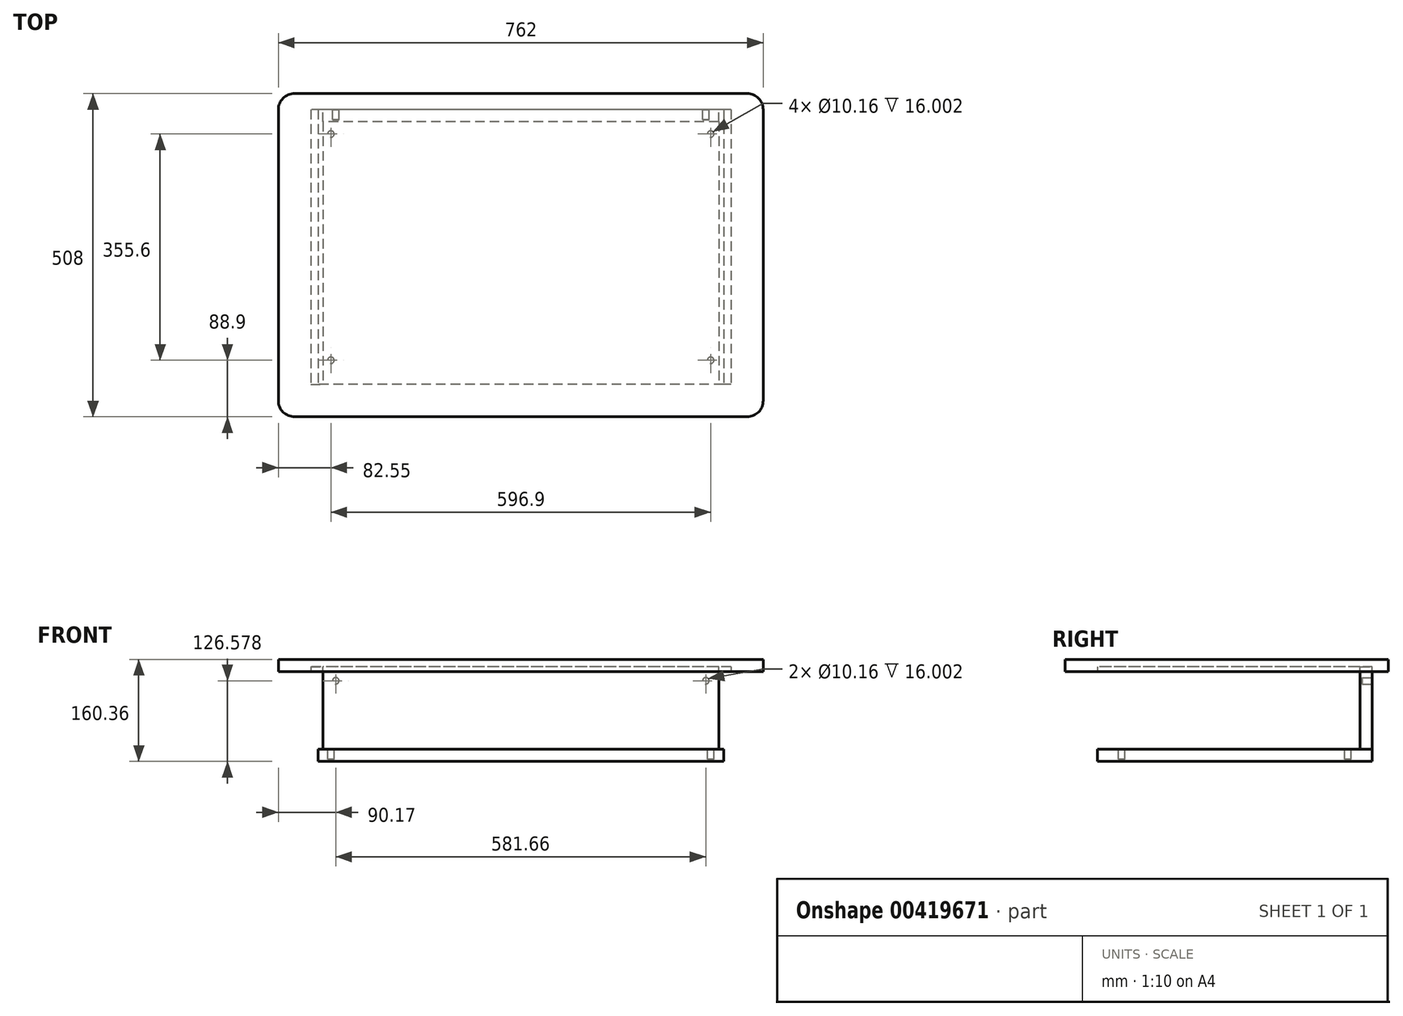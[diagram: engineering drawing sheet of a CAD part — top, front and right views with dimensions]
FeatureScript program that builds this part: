
annotation { "Feature Type Name" : "Feature", "Feature Type Description" : "" }
export const myFeature = defineFeature(function(context is Context, id is Id, definition is map)
    precondition{}
    {
        {
            var Q0;
            Q0=qCreatedBy(makeId("Top.planeOp"),FACE);
            var sketch = newSketch(context, id + "F0", { "sketchPlane" : qUnion([Q0])});
            skLineSegment(sketch, "E0.bottom", {"start": v(-355.6, 254) * mm, "end": v(355.6, 254) * mm});
            skLineSegment(sketch, "E0.top", {"start": v(-355.6, -254) * mm, "end": v(355.6, -254) * mm});
            skLineSegment(sketch, "E0.left", {"start": v(-381, 228.6) * mm, "end": v(-381, -228.6) * mm});
            skLineSegment(sketch, "E0.right", {"start": v(381, 228.6) * mm, "end": v(381, -228.6) * mm});
            skPoint(sketch, "E0.middle", {"position": v(0, 0) * mm});
            skPoint(sketch, "E1.visualSharp", {"position": v(381, 254) * mm});
            skArc(sketch, "E1.filletArc", {"start": v(381, 228.6) * mm, "mid": v(373.56, 246.56) * mm, "end": v(355.6, 254) * mm});
            skPoint(sketch, "E2.visualSharp", {"position": v(381, -254) * mm});
            skArc(sketch, "E2.filletArc", {"start": v(355.6, -254) * mm, "mid": v(373.56, -246.56) * mm, "end": v(381, -228.6) * mm});
            skPoint(sketch, "E3.visualSharp", {"position": v(-381, -254) * mm});
            skArc(sketch, "E3.filletArc", {"start": v(-381, -228.6) * mm, "mid": v(-373.56, -246.56) * mm, "end": v(-355.6, -254) * mm});
            skPoint(sketch, "E4.visualSharp", {"position": v(-381, 254) * mm});
            skArc(sketch, "E4.filletArc", {"start": v(-355.6, 254) * mm, "mid": v(-373.56, 246.56) * mm, "end": v(-381, 228.6) * mm});
            skSolve(sketch);
        }
        {
            var Q0;
            Q0=qSketchRegion(id+"F0",true);
            extrude(context, id + "F1", {"entities" : qUnion([Q0]), "depth" : 19.05 * mm, "offsetDistance" : 25.4 * mm});
        }
        {
            var Q0;
            Q0=makeQuery(id+"F1.opExtrude","CAP_FACE",FACE,{"disambiguationData":[OSD([sQuery(id+"F0.wireOp",EDGE,"E0.bottom"),sQuery(id+"F0.wireOp",EDGE,"E0.top"),sQuery(id+"F0.wireOp",EDGE,"E0.left"),sQuery(id+"F0.wireOp",EDGE,"E0.right"),sQuery(id+"F0.wireOp",EDGE,"E1.filletArc"),sQuery(id+"F0.wireOp",EDGE,"E2.filletArc"),sQuery(id+"F0.wireOp",EDGE,"E3.filletArc"),sQuery(id+"F0.wireOp",EDGE,"E4.filletArc")])],"isStart":true});
            var sketch = newSketch(context, id + "F2", { "sketchPlane" : qUnion([Q0])});
            skLineSegment(sketch, "E5.bottom", {"start": v(330.2, -228.6) * mm, "end": v(-330.2, -228.6) * mm});
            skLineSegment(sketch, "E5.top", {"start": v(330.2, -209.55) * mm, "end": v(-330.2, -209.55) * mm});
            skLineSegment(sketch, "E5.left", {"start": v(330.2, -228.6) * mm, "end": v(330.2, -209.55) * mm});
            skLineSegment(sketch, "E5.right", {"start": v(-330.2, -228.6) * mm, "end": v(-330.2, -209.55) * mm});
            skLineSegment(sketch, "E6.top", {"start": v(330.2, 203.2) * mm, "end": v(311.15, 203.2) * mm});
            skLineSegment(sketch, "E6.left", {"start": v(330.2, -209.55) * mm, "end": v(330.2, 203.2) * mm});
            skLineSegment(sketch, "E6.right", {"start": v(311.15, -209.55) * mm, "end": v(311.15, 203.2) * mm});
            skLineSegment(sketch, "E7.bottom", {"start": v(-330.2, -209.55) * mm, "end": v(-311.15, -209.55) * mm});
            skLineSegment(sketch, "E7.top", {"start": v(-330.2, 203.2) * mm, "end": v(-311.15, 203.2) * mm});
            skLineSegment(sketch, "E7.left", {"start": v(-330.2, -209.55) * mm, "end": v(-330.2, 203.2) * mm});
            skLineSegment(sketch, "E7.right", {"start": v(-311.15, -209.55) * mm, "end": v(-311.15, 203.2) * mm});
            skSolve(sketch);
        }
        {
            var Q0;
            Q0=qSketchRegion(id+"F2",true);
            extrude(context, id + "F3", {"entities" : qUnion([Q0]), "operationType" : NewBodyOperationType.REMOVE, "oppositeDirection" : true, "depth" : 7.62 * mm});
        }
        {
            var Q0;
            Q0=makeQuery(id+"F3.boolean.opBoolean","COPY",FACE,{"derivedFrom":makeQuery(id+"F3.opExtrude","CAP_FACE",FACE,{"disambiguationData":[OSD([sQuery(id+"F2.wireOp",EDGE,"E5.bottom"),sQuery(id+"F2.wireOp",EDGE,"E5.top"),sQuery(id+"F2.wireOp",EDGE,"E5.left"),sQuery(id+"F2.wireOp",EDGE,"E5.right"),sQuery(id+"F2.wireOp",EDGE,"E6.top"),sQuery(id+"F2.wireOp",EDGE,"E6.left"),sQuery(id+"F2.wireOp",EDGE,"E6.right"),sQuery(id+"F2.wireOp",EDGE,"E7.top"),sQuery(id+"F2.wireOp",EDGE,"E7.left"),sQuery(id+"F2.wireOp",EDGE,"E7.right")])],"isStart":false})});
            var sketch = newSketch(context, id + "F4", { "sketchPlane" : qUnion([Q0])});
            skLineSegment(sketch, "E8.bottom", {"start": v(311.15, -209.55) * mm, "end": v(-311.15, -209.55) * mm});
            skLineSegment(sketch, "E8.top", {"start": v(311.15, -228.6) * mm, "end": v(-311.15, -228.6) * mm});
            skLineSegment(sketch, "E8.left", {"start": v(311.15, -209.55) * mm, "end": v(311.15, -228.6) * mm});
            skLineSegment(sketch, "E8.right", {"start": v(-311.15, -209.55) * mm, "end": v(-311.15, -228.6) * mm});
            skSolve(sketch);
        }
        {
            var Q0;
            Q0=makeQuery(id+"F4.imprint","IMPRINT",FACE,{"disambiguationData":[TD([[makeQuery(id+"F4.imprint","IMPRINT",EDGE,{"derivedFrom":sQuery(id+"F4.wireOp",EDGE,"E8.bottom")}),1.0]])]});
            extrude(context, id + "F5", {"entities" : qUnion([Q0]), "depth" : 129.88 * mm});
        }
        {
            var Q0;
            Q0=makeQuery(id+"F5.opExtrude","CAP_FACE",FACE,{"disambiguationData":[OSD([sQuery(id+"F4.wireOp",EDGE,"E8.bottom"),sQuery(id+"F4.wireOp",EDGE,"E8.top"),sQuery(id+"F4.wireOp",EDGE,"E8.left"),sQuery(id+"F4.wireOp",EDGE,"E8.right")])],"isStart":false});
            var sketch = newSketch(context, id + "F6", { "sketchPlane" : qUnion([Q0])});
            skLineSegment(sketch, "E9.bottom", {"start": v(318.77, -228.6) * mm, "end": v(-318.77, -228.6) * mm});
            skLineSegment(sketch, "E9.top", {"start": v(318.77, 203.2) * mm, "end": v(-318.77, 203.2) * mm});
            skLineSegment(sketch, "E9.left", {"start": v(318.77, -228.6) * mm, "end": v(318.77, 203.2) * mm});
            skLineSegment(sketch, "E9.right", {"start": v(-318.77, -228.6) * mm, "end": v(-318.77, 203.2) * mm});
            skSolve(sketch);
        }
        {
            var Q0;
            Q0=qSketchRegion(id+"F6",true);
            extrude(context, id + "F7", {"entities" : qUnion([Q0]), "depth" : 19.05 * mm});
        }
        {
            var Q0;
            Q0=makeQuery(id+"F5.opExtrude","SWEPT_FACE",FACE,{"disambiguationData":[OSD([sQuery(id+"F4.wireOp",EDGE,"E8.top")])]});
            var sketch = newSketch(context, id + "F8", { "sketchPlane" : qUnion([Q0])});
            skCircle(sketch, "E10", {"center": v(-290.83, -14.73) * mm, "radius": 5.08 * mm});
            skCircle(sketch, "E11", {"center": v(290.83, -14.73) * mm, "radius": 5.08 * mm});
            skSolve(sketch);
        }
        {
            var Q0;
            Q0=qSketchRegion(id+"F8",true);
            extrude(context, id + "F9", {"entities" : qUnion([Q0]), "operationType" : NewBodyOperationType.REMOVE, "oppositeDirection" : true, "depth" : 16 * mm});
        }
        {
            var Q0;
            Q0=makeQuery(id+"F7.opExtrude","CAP_FACE",FACE,{"disambiguationData":[OSD([sQuery(id+"F6.wireOp",EDGE,"E9.bottom"),sQuery(id+"F6.wireOp",EDGE,"E9.top"),sQuery(id+"F6.wireOp",EDGE,"E9.left"),sQuery(id+"F6.wireOp",EDGE,"E9.right")])],"isStart":true});
            var sketch = newSketch(context, id + "F10", { "sketchPlane" : qUnion([Q0])});
            skCircle(sketch, "E12", {"center": v(-298.45, 190.5) * mm, "radius": 5.08 * mm});
            skCircle(sketch, "E13", {"center": v(298.45, 190.5) * mm, "radius": 5.08 * mm});
            skCircle(sketch, "E14", {"center": v(298.45, -165.1) * mm, "radius": 5.08 * mm});
            skCircle(sketch, "E15", {"center": v(-298.45, -165.1) * mm, "radius": 5.08 * mm});
            skSolve(sketch);
        }
        {
            var Q0;
            Q0=qSketchRegion(id+"F10",true);
            extrude(context, id + "F11", {"entities" : qUnion([Q0]), "operationType" : NewBodyOperationType.REMOVE, "oppositeDirection" : true, "depth" : 16 * mm});
        }
    });
